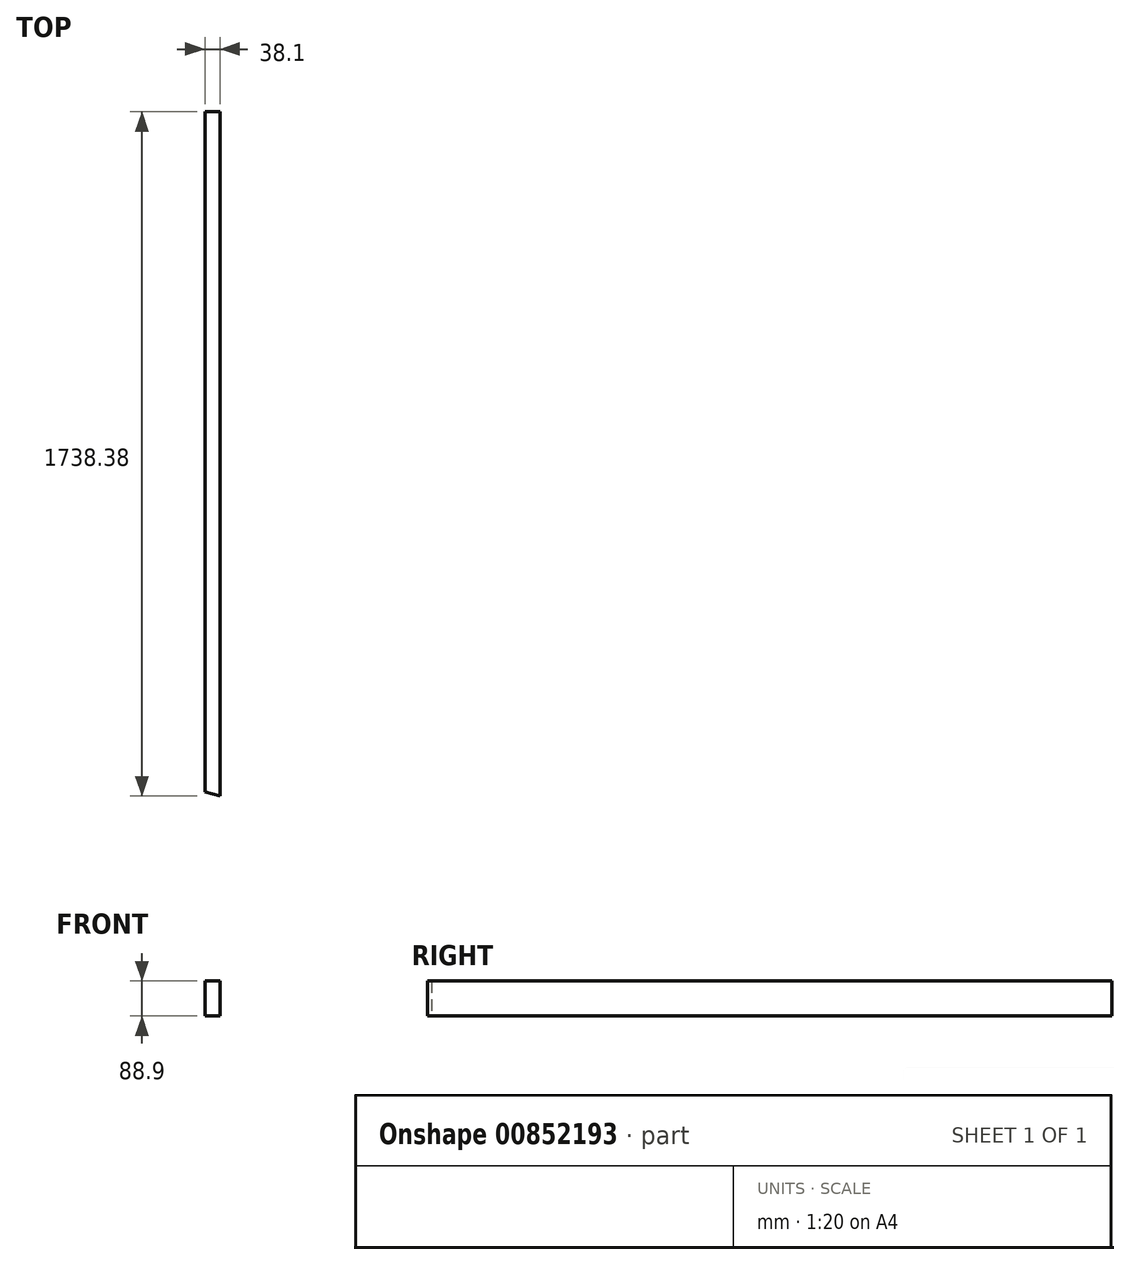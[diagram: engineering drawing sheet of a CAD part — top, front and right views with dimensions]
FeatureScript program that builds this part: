
annotation { "Feature Type Name" : "Feature", "Feature Type Description" : "" }
export const myFeature = defineFeature(function(context is Context, id is Id, definition is map)
    precondition{}
    {
        {
            var Q0;
            Q0=qCreatedBy(makeId("Front.planeOp"),FACE);
            var sketch = newSketch(context, id + "F0", { "sketchPlane" : qUnion([Q0])});
            skLineSegment(sketch, "E0.bottom", {"start": v(19.05, -44.45) * mm, "end": v(-19.05, -44.45) * mm});
            skLineSegment(sketch, "E0.top", {"start": v(19.05, 44.45) * mm, "end": v(-19.05, 44.45) * mm});
            skLineSegment(sketch, "E0.left", {"start": v(19.05, -44.45) * mm, "end": v(19.05, 44.45) * mm});
            skLineSegment(sketch, "E0.right", {"start": v(-19.05, -44.45) * mm, "end": v(-19.05, 44.45) * mm});
            skPoint(sketch, "E0.middle", {"position": v(0, 0) * mm});
            skSolve(sketch);
        }
        {
            var Q0;
            Q0=makeQuery(id+"F0.imprint","IMPRINT",FACE,{"disambiguationData":[TD([[makeQuery(id+"F0.imprint","IMPRINT",EDGE,{"derivedFrom":sQuery(id+"F0.wireOp",EDGE,"E0.bottom")}),-1.0]])]});
            var Q1;
            Q1=qSketchRegion(id+"F2",true);
            extrude(context, id + "F1", {"entities" : qUnion([Q0, Q1]), "depth" : 1738.38 * mm, "offsetDistance" : 25.4 * mm});
        }
        {
            var Q0;
            Q0=qCreatedBy(makeId("Top.planeOp"),FACE);
            var sketch = newSketch(context, id + "F2", { "sketchPlane" : qUnion([Q0])});
            skLineSegment(sketch, "E1", {"start": v(19.05, -1738.38) * mm, "end": v(-19.05, -1738.38) * mm});
            skLineSegment(sketch, "E2", {"start": v(-19.05, -1738.38) * mm, "end": v(-19.05, -1728.17) * mm});
            skLineSegment(sketch, "E3", {"start": v(-19.05, -1728.17) * mm, "end": v(19.05, -1738.38) * mm});
            skSolve(sketch);
        }
        {
            var Q0;
            Q0=qSketchRegion(id+"F2",true);
            extrude(context, id + "F3", {"entities" : qUnion([Q0]), "operationType" : NewBodyOperationType.REMOVE, "endBound" : BoundingType.SYMMETRIC, "depth" : 127 * mm, "offsetDistance" : 25.4 * mm});
        }
    });
